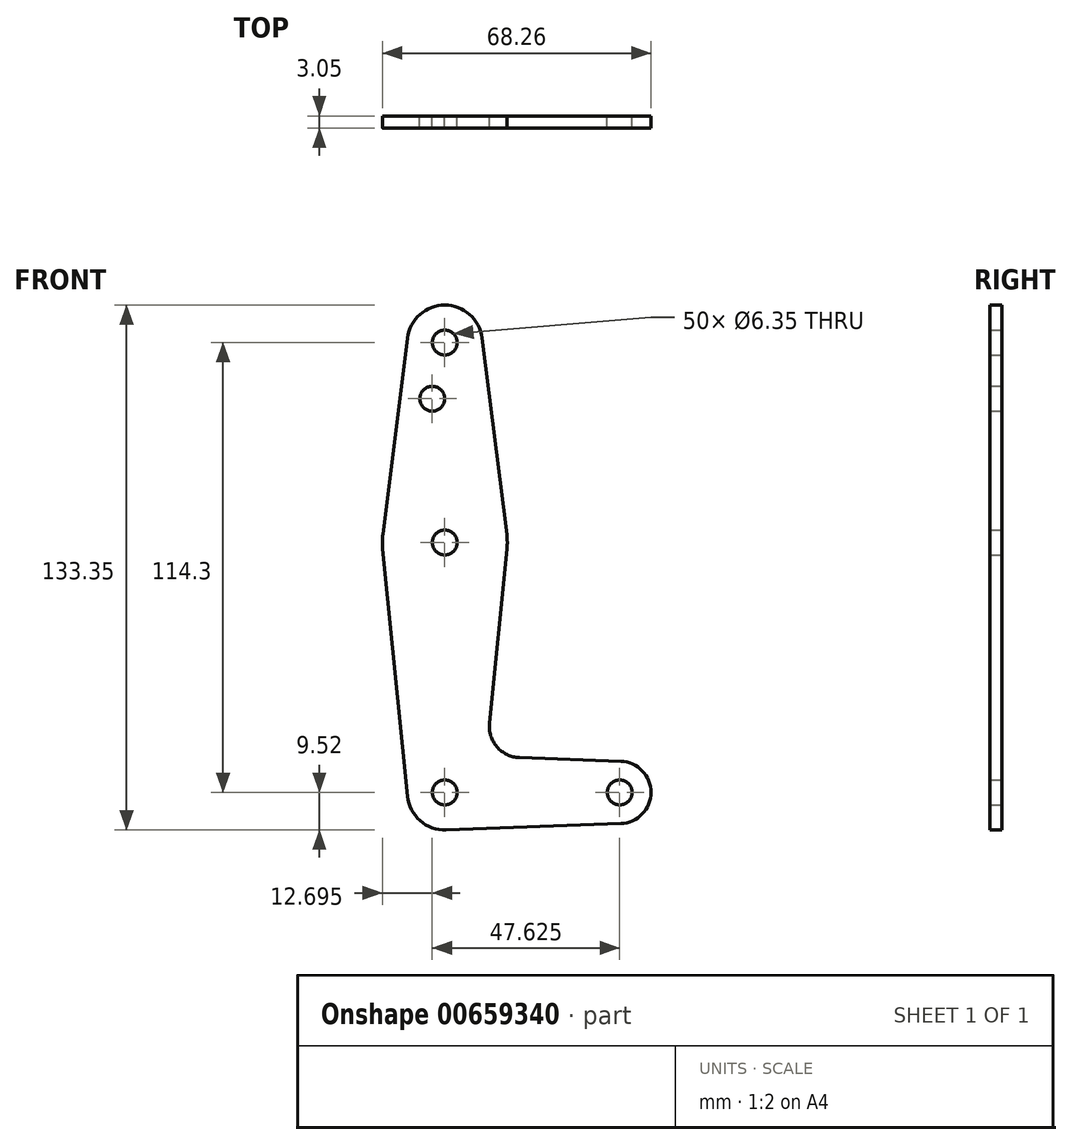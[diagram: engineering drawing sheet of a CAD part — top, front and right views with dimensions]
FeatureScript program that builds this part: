
annotation { "Feature Type Name" : "Feature", "Feature Type Description" : "" }
export const myFeature = defineFeature(function(context is Context, id is Id, definition is map)
    precondition{}
    {
        {
            var Q0;
            Q0=qCreatedBy(makeId("Front.planeOp"),FACE);
            var sketch = newSketch(context, id + "F0", { "sketchPlane" : qUnion([Q0])});
            skCircle(sketch, "E0", {"center": v(0, 63.5) * mm, "radius": 15.88 * mm});
            skCircle(sketch, "E1", {"center": v(44.45, 0) * mm, "radius": 7.94 * mm});
            skCircle(sketch, "E2", {"center": v(0, 114.3) * mm, "radius": 9.53 * mm});
            skLineSegment(sketch, "E3", {"start": v(0, 0) * mm, "end": v(0, 114.3) * mm, "construction": true});
            skLineSegment(sketch, "E4", {"start": v(0, 0) * mm, "end": v(44.45, 0) * mm, "construction": true});
            skCircle(sketch, "E5", {"center": v(0, 0) * mm, "radius": 9.53 * mm});
            skLineSegment(sketch, "E6", {"start": v(-9.45, 115.5) * mm, "end": v(-15.75, 65.48) * mm});
            skLineSegment(sketch, "E7", {"start": v(9.45, 115.5) * mm, "end": v(15.75, 65.48) * mm});
            skLineSegment(sketch, "E8", {"start": v(-15.8, 61.91) * mm, "end": v(-9.48, -0.95) * mm});
            skLineSegment(sketch, "E9", {"start": v(15.8, 61.91) * mm, "end": v(11.34, 17.6) * mm});
            skLineSegment(sketch, "E10", {"start": v(44.73, 7.93) * mm, "end": v(18.97, 8.85) * mm});
            skLineSegment(sketch, "E11", {"start": v(0.34, -9.52) * mm, "end": v(44.73, -7.93) * mm});
            skCircle(sketch, "E12", {"center": v(-3.18, 100.03) * mm, "radius": 3.18 * mm});
            skCircle(sketch, "E13", {"center": v(0, 114.3) * mm, "radius": 3.18 * mm});
            skCircle(sketch, "E14", {"center": v(0, 63.5) * mm, "radius": 3.18 * mm});
            skCircle(sketch, "E15", {"center": v(0, 0) * mm, "radius": 3.18 * mm});
            skCircle(sketch, "E16", {"center": v(44.45, 0) * mm, "radius": 3.18 * mm});
            skArc(sketch, "E17.filletArc", {"start": v(11.34, 17.6) * mm, "mid": v(13.26, 11.57) * mm, "end": v(18.97, 8.85) * mm});
            skSolve(sketch);
        }
        {
            var Q0;
            Q0 = qSketchRegion(id + "F0", true);
            extrude(context, id + "F1", {"entities" : qUnion([Q0]), "depth" : 3.05 * mm, "offsetDistance" : 25.4 * mm});
        }
    });
